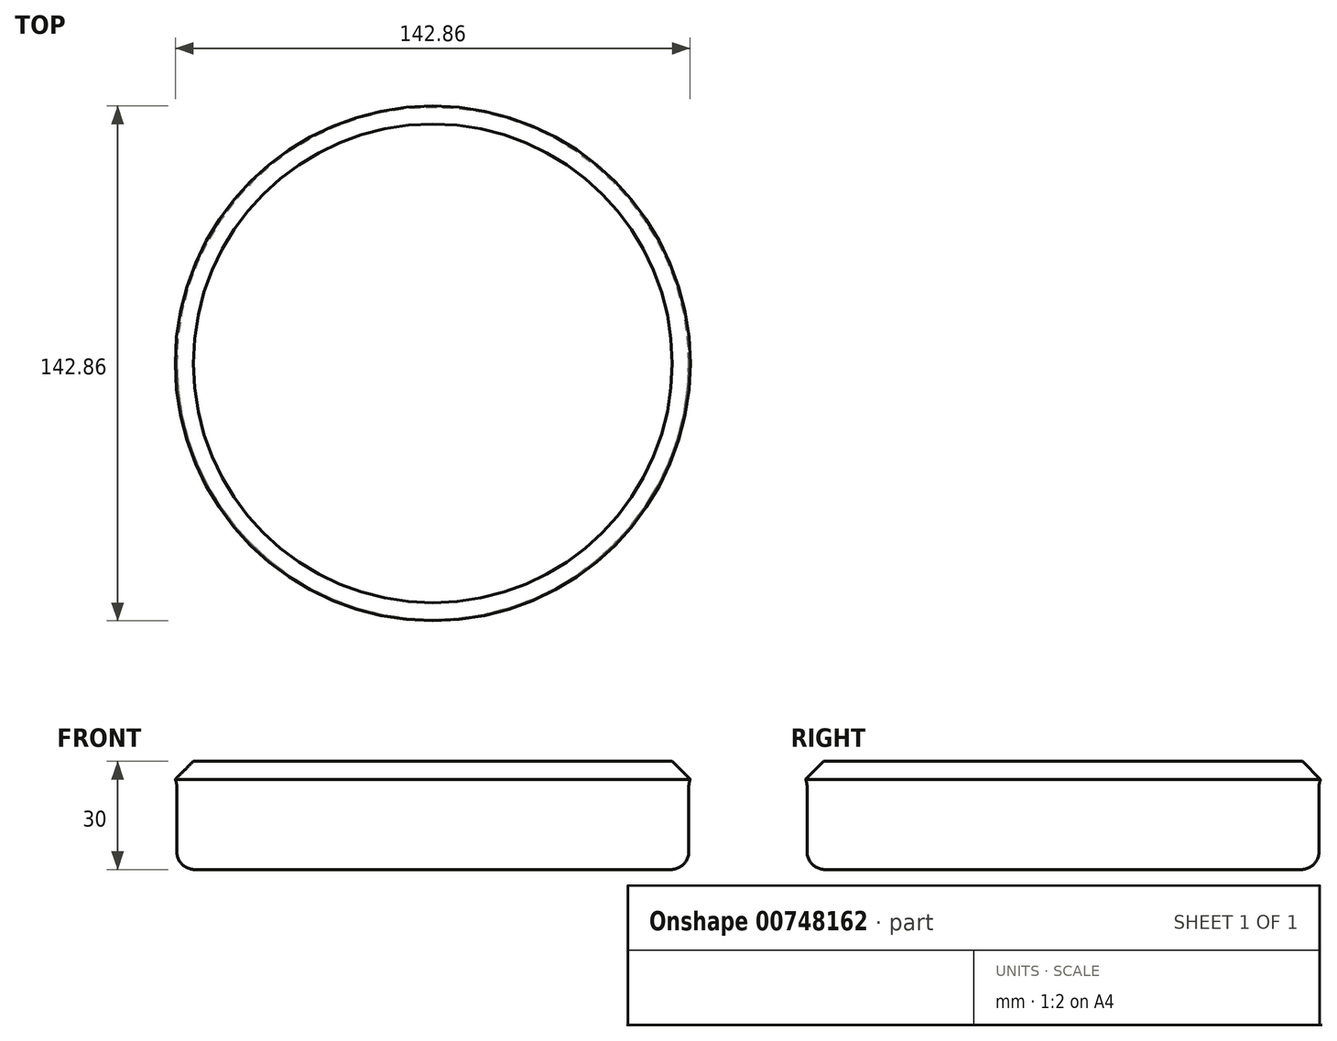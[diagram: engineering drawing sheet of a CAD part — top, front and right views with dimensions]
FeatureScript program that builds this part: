
annotation { "Feature Type Name" : "Feature", "Feature Type Description" : "" }
export const myFeature = defineFeature(function(context is Context, id is Id, definition is map)
    precondition{}
    {
        {
            var Q0;
            Q0=qCreatedBy(makeId("Top.planeOp"),FACE);
            var sketch = newSketch(context, id + "F0", { "sketchPlane" : qUnion([Q0])});
            skLineSegment(sketch, "E0.bottom", {"start": v(-43.13, 21.53) * mm, "end": v(42.01, 21.53) * mm});
            skLineSegment(sketch, "E0.top", {"start": v(-43.13, -24.79) * mm, "end": v(42.01, -24.79) * mm});
            skLineSegment(sketch, "E0.left", {"start": v(-43.13, 21.53) * mm, "end": v(-43.13, -24.79) * mm});
            skLineSegment(sketch, "E0.right", {"start": v(42.01, 21.53) * mm, "end": v(42.01, -24.79) * mm});
            skSolve(sketch);
        }
        {
            var Q0;
            Q0=makeQuery(id+"F0.imprint","IMPRINT",FACE,{"disambiguationData":[TD([[makeQuery(id+"F0.imprint","IMPRINT",EDGE,{"derivedFrom":sQuery(id+"F0.wireOp",EDGE,"E0.bottom")}),-1.0]])]});
            var sketch = newSketch(context, id + "F1", { "sketchPlane" : qUnion([Q0])});
            skLineSegment(sketch, "E1", {"start": v(-43.13, 16.53) * mm, "end": v(-38.37, 21.03) * mm});
            skSolve(sketch);
        }
        {
            var Q0;
            Q0=qCreatedBy(makeId("Top.planeOp"),FACE);
            var sketch = newSketch(context, id + "F2", { "sketchPlane" : qUnion([Q0])});
            skCircle(sketch, "E2", {"center": v(0, 0) * mm, "radius": 71.44 * mm});
            skSolve(sketch);
        }
        {
            var Q0;
            Q0=makeQuery(id+"F2.imprint","IMPRINT",FACE,{"disambiguationData":[TD([[makeQuery(id+"F2.imprint","IMPRINT",EDGE,{"derivedFrom":sQuery(id+"F2.wireOp",EDGE,"E2")}),1.0]])]});
            extrude(context, id + "F3", {"entities" : qUnion([Q0]), "depth" : 5 * mm, "offsetDistance" : 25 * mm});
        }
        {
            var Q0;
            Q0=makeQuery(id+"F3.opExtrude","CAP_FACE",FACE,{"disambiguationData":[OSD([sQuery(id+"F2.wireOp",EDGE,"E2")])],"isStart":true});
            var sketch = newSketch(context, id + "F4", { "sketchPlane" : qUnion([Q0])});
            skCircle(sketch, "E3", {"center": v(0, 0) * mm, "radius": 71.03 * mm});
            skSolve(sketch);
        }
        {
            var Q0;
            Q0=makeQuery(id+"F3.opExtrude","CAP_FACE",FACE,{"disambiguationData":[OSD([sQuery(id+"F2.wireOp",EDGE,"E2")])],"isStart":false});
            var sketch = newSketch(context, id + "F5", { "sketchPlane" : qUnion([Q0])});
            skCircle(sketch, "E4", {"center": v(0, 0) * mm, "radius": 54.7 * mm});
            skSolve(sketch);
        }
        {
            var Q0;
            Q0 = qSketchRegion(id + "F4", true);
            extrude(context, id + "F6", {"entities" : qUnion([Q0]), "operationType" : NewBodyOperationType.ADD, "depth" : 25 * mm, "offsetDistance" : 25 * mm});
        }
        {
            var Q0;
            Q0=makeQuery(id+"F3.opExtrude","CAP_EDGE",EDGE,{"disambiguationData":[OSD([sQuery(id+"F2.wireOp",EDGE,"E2")])],"isStart":true});
            fillet(context, id + "F7", {"entities" : qUnion([Q0]), "radius" : 0.02 * mm, "tangentPropagation" : true, "allowEdgeOverflow" : false});
        }
        {
            var Q0;
            Q0=makeQuery(id+"F3.opExtrude","CAP_EDGE",EDGE,{"disambiguationData":[OSD([sQuery(id+"F2.wireOp",EDGE,"E2")])],"isStart":false});
            chamfer(context, id + "F8", {"entities" : qUnion([Q0]), "width" : 5 * mm, "tangentPropagation" : true});
        }
        {
            var Q0;
            Q0=makeQuery(id+"F6.opExtrude","SWEPT_FACE",FACE,{"disambiguationData":[OSD([sQuery(id+"F4.wireOp",EDGE,"E3")])]});
            fillet(context, id + "F9", {"entities" : qUnion([Q0]), "radius" : 5 * mm, "tangentPropagation" : true, "allowEdgeOverflow" : false});
        }
    });
